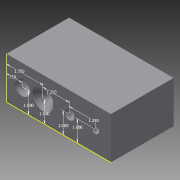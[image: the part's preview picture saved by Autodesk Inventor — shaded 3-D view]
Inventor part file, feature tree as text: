
AUTODESK INVENTOR PART (.ipt)
format: ipt  version: 2015 (Build 190159000, 159)  size: 108,032 bytes
history: native  units: in
note: dims shown in document units (in); Inventor stores cm internally (conversion verified against a paired STEP export)
features: hole x4, sketch x2, extrude x1
ambient origin geometry x8: Origin, YZ Plane, XZ Plane, XY Plane, X Axis, Y Axis, Z Axis, Center Point
bodies: Solid1 (feature_tree)
feature tree (7):
  extrude  "Extrusion1"  Depth=5.0in
  sketch  "Sketch2"  dims[d2=3.0in d3=0.0in d4=1.0in d5=1.0in d6=1.0in d7=1.0in d8=0.75in d9=1.75in d10=1.25in d11=1.25in d12=0.25in d13=0.75in d14=0.375in d15=0.25in d16=0.5635in d17=1.0in d18=0.8108in d19=0.5in d20=1.0in d21=0.375in d22=0.25in d23=0.5635in d24=1.0in d25=0.8108in d26=0.5in d27=1.0in d28=1.0in d29=0.25in d30=0.5635in d31=1.0in d32=0.8108in d33=0.5in d34=1.0in d35=0.75in d36=0.5in d37=0.5635in d38=2.0in d39=0.8108in]
  hole  "Hole1"  [1 undecoded]
  hole  "Hole2"  [1 undecoded]
  hole  "Hole3"  [1 undecoded]
  hole  "Hole4"  [1 undecoded]
  sketch  "Sketch1"  dims[d0=2.0in d1=5.0in]
note: 4 required parameter values undecoded (feature->parameter linkage not recoverable at this tier; creation-order binding heuristic only, values carry confidence <= 0.55)
